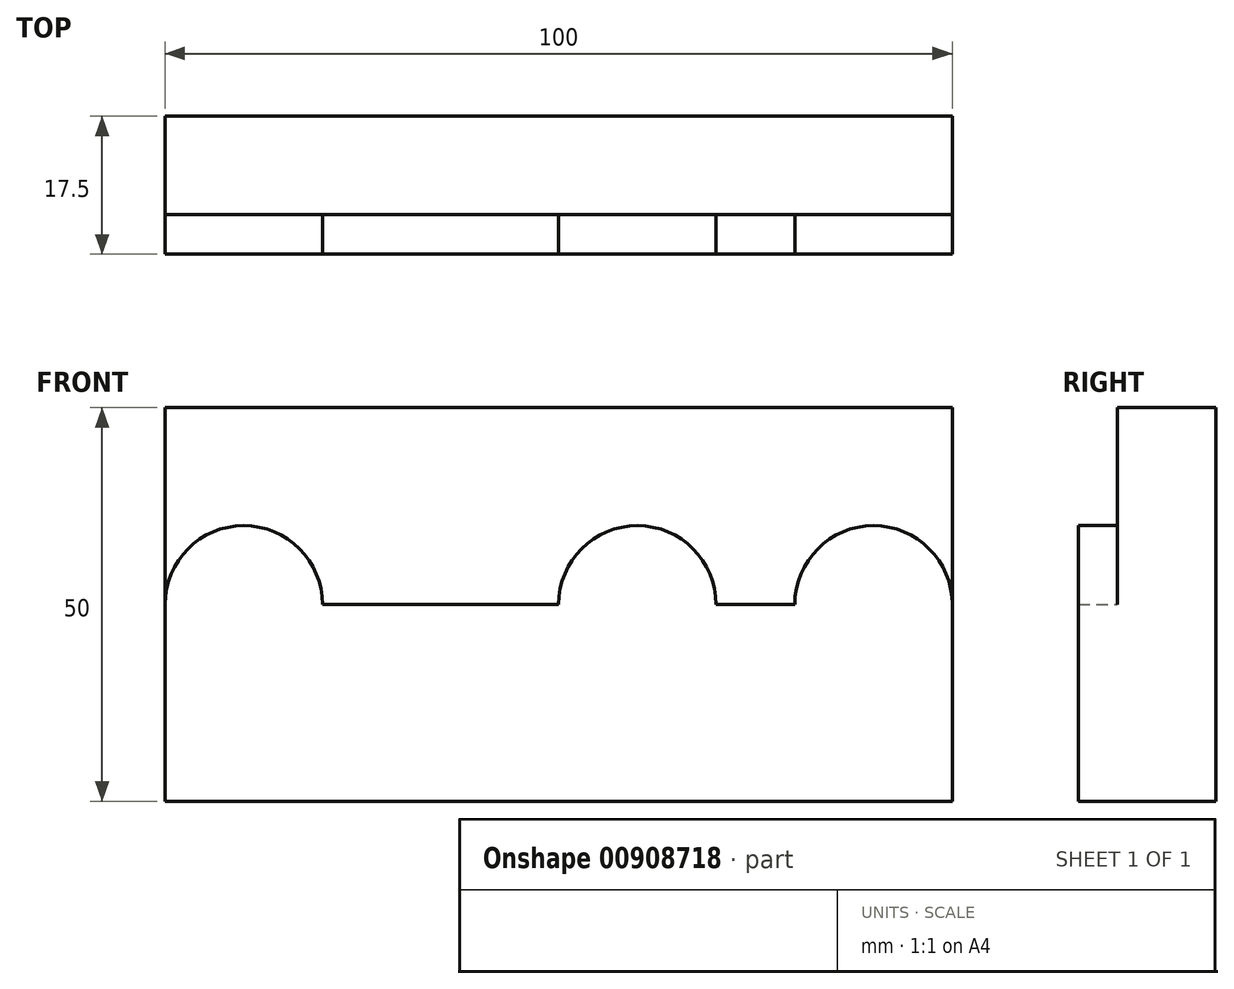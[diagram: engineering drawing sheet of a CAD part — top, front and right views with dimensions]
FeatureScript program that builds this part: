
annotation { "Feature Type Name" : "Feature", "Feature Type Description" : "" }
export const myFeature = defineFeature(function(context is Context, id is Id, definition is map)
    precondition{}
    {
        {
            var Q0;
            Q0=qCreatedBy(makeId("Front.planeOp"),FACE);
            var sketch = newSketch(context, id + "F0", { "sketchPlane" : qUnion([Q0])});
            skLineSegment(sketch, "E0.bottom", {"start": v(0, 0) * mm, "end": v(100, 0) * mm});
            skLineSegment(sketch, "E0.top", {"start": v(0, 50) * mm, "end": v(100, 50) * mm});
            skLineSegment(sketch, "E0.left", {"start": v(0, 0) * mm, "end": v(0, 50) * mm});
            skLineSegment(sketch, "E0.right", {"start": v(100, 0) * mm, "end": v(100, 50) * mm});
            skSolve(sketch);
        }
        {
            var Q0;
            Q0 = qSketchRegion(id + "F0", true);
            extrude(context, id + "F1", {"entities" : qUnion([Q0]), "depth" : 12.5 * mm, "offsetDistance" : 25 * mm});
        }
        {
            var Q0;
            Q0=makeQuery(id+"F1.opExtrude","CAP_FACE",FACE,{"disambiguationData":[OSD([sQuery(id+"F0.wireOp",EDGE,"E0.bottom"),sQuery(id+"F0.wireOp",EDGE,"E0.top"),sQuery(id+"F0.wireOp",EDGE,"E0.left"),sQuery(id+"F0.wireOp",EDGE,"E0.right")])],"isStart":false});
            var sketch = newSketch(context, id + "F2", { "sketchPlane" : qUnion([Q0])});
            skLineSegment(sketch, "E1", {"start": v(0, 25) * mm, "end": v(0, 0) * mm});
            skLineSegment(sketch, "E2", {"start": v(0, 0) * mm, "end": v(100, 0) * mm});
            skLineSegment(sketch, "E3", {"start": v(100, 0) * mm, "end": v(100, 25) * mm});
            skLineSegment(sketch, "E4", {"start": v(100, 25) * mm, "end": v(80, 25) * mm});
            skLineSegment(sketch, "E5", {"start": v(80, 25) * mm, "end": v(70, 25) * mm});
            skLineSegment(sketch, "E6", {"start": v(20, 25) * mm, "end": v(0, 25) * mm});
            skArc(sketch, "E7", {"start": v(100, 25) * mm, "mid": v(90, 35) * mm, "end": v(80, 25) * mm});
            skArc(sketch, "E8", {"start": v(20, 25) * mm, "mid": v(10, 35) * mm, "end": v(0, 25) * mm});
            skLineSegment(sketch, "E9", {"start": v(70, 25) * mm, "end": v(50, 25) * mm});
            skLineSegment(sketch, "E10", {"start": v(50, 25) * mm, "end": v(20, 25) * mm});
            skArc(sketch, "E11", {"start": v(70, 25) * mm, "mid": v(60, 35) * mm, "end": v(50, 25) * mm});
            skSolve(sketch);
        }
        {
            var Q0;
            Q0 = qSketchRegion(id + "F2", true);
            extrude(context, id + "F3", {"entities" : qUnion([Q0]), "operationType" : NewBodyOperationType.ADD, "depth" : 5 * mm, "offsetDistance" : 25 * mm});
        }
    });
